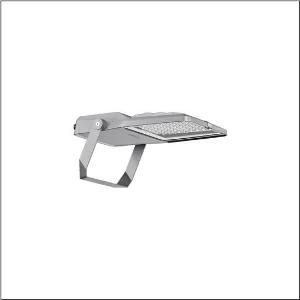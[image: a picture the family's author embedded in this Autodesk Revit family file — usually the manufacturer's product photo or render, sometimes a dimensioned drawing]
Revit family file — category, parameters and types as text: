
# Revit family: floodlight_fl_21_iq_mini___pl43_5xa7772c2a1a_250e
name_source: partatom
category: Lighting Fixtures
units: mm (PartAtom-declared; Revit-internal decimal feet)

## family parameters
Cut with Voids When Loaded = No
Host = Face
Light Source = No
Part Type = Normal
Room Calculation Point = No
Round Connector Dimension = Use Diameter
Shared = No

## types (1)
- --- (1 x LED, 12520 lm, 87.2 W, 3000K)
    Apparent Load = 87 VA
    CIE Flux Codes = 27 78 99 100 100
    Color Rendering = 70
    Color Temperature = 3000K
    Default Elevation = 1800 mm
    Description = Floodlight FL 21 iQ mini, floodlight, primary light control with lens, of PMMA, primary optical cover: protective disc, of toughened safety glass, transparent, light distribution: PL43, light emission: direct distribution, installation type: surface-mounted, LED, High Power LED, rated luminous flux: 12.520lm, luminous efficacy: 144lm/W, light colour: 730, colour temperature: 3000K, control: Street-Remote, Auto-Match, Temp-Guard, Night-Set, Smart-Wire, Desk-Remote (wireless, voltage-free reading and setting of iQ features in the workshop via application-optimized NFC function/RFID function), optimised constant luminous flux control (CLO 2.0), with terminal, 6-pole, mains connection: 220..240V, AC, 50/60Hz, start of lifetime: 87W, end of service life: 92W, reduction: 40W, luminaire housing, of diecast aluminium, powder-coated, Siteco® metallic grey (DB 702S), corrosivity category C5 mid according to DIN EN ISO 12944, sealing non-destructively replaceable, mounting bracket, of steel, galvanised, powder-coated, Siteco® metallic grey (DB 702S), protection rating (complete): IP66, insulation class (complete): insulation class II (safety insulation), certification: CE, ENEC, VDE, protection symbol: D, impact resistance: IK08, permissible operating ambient temperature: -40..+40°C, permissible operating ambient temperature for outdoor applications: -40..+50°C, standard: DIN EN 12944, LABS conformity tested according to VDMA 24364:2018-05, packaging unit: 1 piece

Light Distribution: PL43
    Height = 70 mm
    Lamp = 1 x LED
    Lamp Light Flux = 12520 lm
    Lamp Power = 87.2 W
    Lamp count = 1
    Length = 485 mm
    Luminous efficacy = 144 lm/W
    Manufacturer = Siteco
    ModVariant = No
    Model = 5XA7772C2A1A
    Number of Poles = 1
    OnlyDefault = Yes
    Power Factor = 1
    Product Name = Floodlight FL 21 iQ mini | PL43
    Product group = floodlight | pylon annexe
    ProductGroupID = 6200
    Protection Class = Protection class II
    Protection Degree = IP 66
    RLX_Detail_Level = 1
    RLX_Emergency_Light_Flux = 0 lm
    RLX_Emergency_Type = 0
    RLX_Emergency_Type_DB = No
    RlxData = <blob elided: 96213 chars, md5=0de4340f>
    Socket = socket
    Standby Power = 0 W
    System Light Flux = 12520 lm
    System Power = 87 W
    Type Comments = factory setting: luminous flux: 100 % | dim-lin: 254 | 456 mA
    Type Image = l_1006845.jpg
    URL = http://relux.com
    VarID = @adj_112725
    Voltage = 0 V
    Weight = 0.00 kg
    Width = 337 mm

## geometry (parser evidence)
native form markers: Blend x4, Sweep x11
no freeform markers — native parametric forms only
